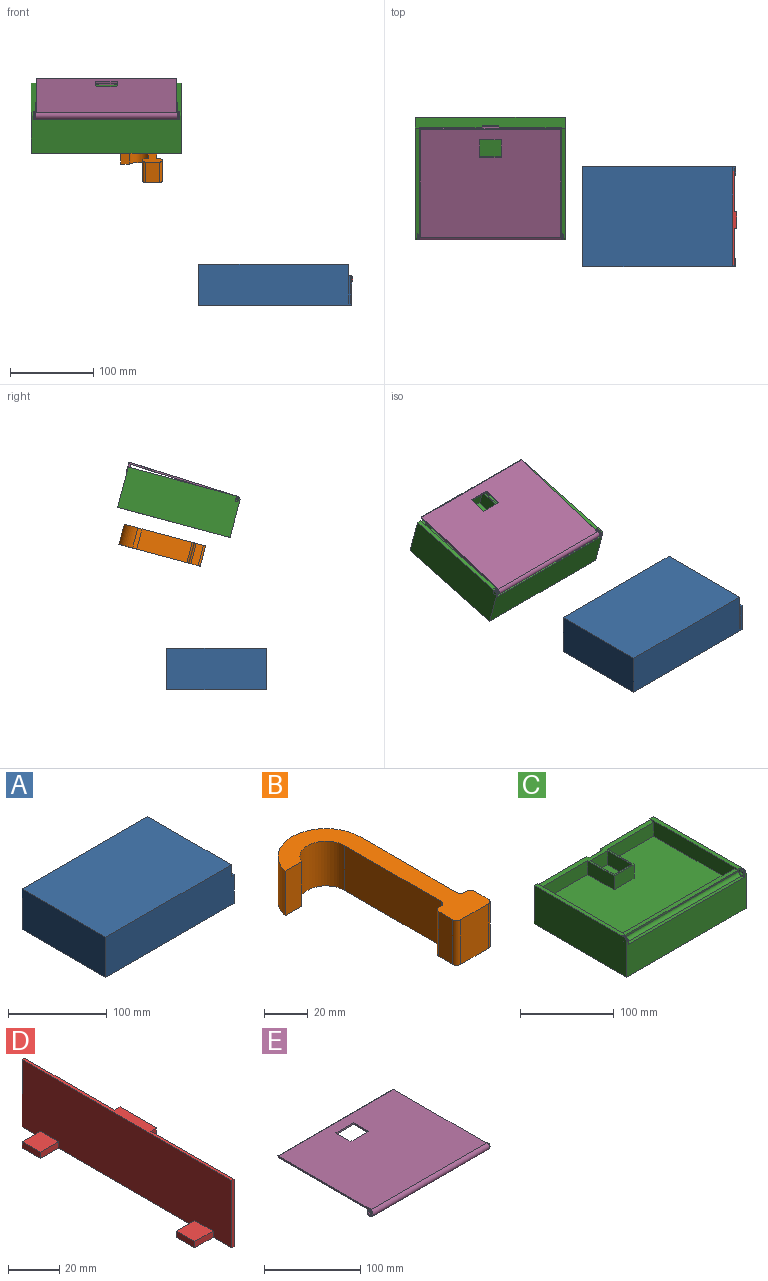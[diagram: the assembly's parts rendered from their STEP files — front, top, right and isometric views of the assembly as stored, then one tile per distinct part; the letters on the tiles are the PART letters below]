
ASSEMBLY  parts=5 mates=3
PART A: 23 faces, bbox 184x120x50 mm
  f0: plane 120x48mm, normal (1,0,0), area 2324mm2, adj f2,f5,f6,f7,f8,f9,f10,f12
  f1: plane 100x2mm, normal (1,0,0), area 200mm2, adj f4,f9,f14,f18
  f2: plane 180x120mm, normal (0,0,1), area 21600mm2, adj f0,f3,f5,f6
  f3: plane 120x50mm, normal (-1,0,0), area 6000mm2, adj f2,f4,f5,f6
  f4: plane 184x120mm, normal (0,0,-1), area 20772.1mm2, adj f1,f3,f5,f6,f14,f15,f17,f18
  f5: plane 184x50mm, normal (0,-1,0), area 9144mm2, adj f0,f2,f3,f4,f15,f16
  f6: plane 184x50mm, normal (0,1,0), area 9144mm2, adj f0,f2,f3,f4,f17,f21
  f7: plane 175x110mm, normal (0,0,-1), area 19250mm2, adj f0,f8,f10,f11
  f8: plane 175x30mm, normal (0,1,0), area 5250mm2, adj f0,f7,f9,f11
  f9: plane 177x116mm, normal (0,0,1), area 18374.1mm2, adj f0,f1,f8,f10,f11,f12,f13,f14
  f10: plane 175x30mm, normal (0,-1,0), area 5250mm2, adj f0,f7,f9,f11
  f11: plane 110x30mm, normal (1,0,0), area 3300mm2, adj f7,f8,f9,f10
  f12: plane 34x2mm, normal (0,1,0), area 68mm2, adj f0,f9,f13,f16
  f13: plane 34x8mm, normal (-1,0,0), area 272mm2, adj f9,f12,f14,f16
  f14: plane 36x4mm, normal (0,1,0), area 76mm2, adj f1,f4,f9,f13,f15,f16
  f15: plane 36x10mm, normal (1,0,0), area 360mm2, adj f4,f5,f14,f16
  f16: plane 10x4mm, normal (0,0,1), area 24mm2, adj f0,f5,f12,f13,f14,f15
  f17: plane 36x10mm, normal (1,0,0), area 360mm2, adj f4,f6,f18,f21
  f18: plane 36x4mm, normal (0,-1,0), area 76mm2, adj f1,f4,f9,f17,f19,f21
  f19: plane 34x8mm, normal (-1,0,0), area 272mm2, adj f9,f18,f20,f21
  f20: plane 34x2mm, normal (0,-1,0), area 68mm2, adj f0,f9,f19,f21
  f21: plane 10x4mm, normal (0,0,1), area 24mm2, adj f0,f6,f17,f18,f19,f20
  f22: cylinder r=17mm len=34mm, axis (0,0,-1), area 213.6mm2, adj f4,f9
PART B: 18 faces, bbox 49.9x101x25 mm
  f0: plane 25x17.98mm, normal (0,-1,0), area 449.5mm2, adj f1,f15,f16,f17
  f1: cylinder r=2.5mm len=25mm, axis (0,0,1), area 98.2mm2, adj f0,f2,f16,f17
  f2: plane 25x9mm, normal (-1,0,0), area 225mm2, adj f1,f3,f16,f17
  f3: cylinder r=2.5mm len=25mm, axis (0,0,1), area 98.2mm2, adj f2,f4,f16,f17
  f4: plane 25x1.5mm, normal (0,1,0), area 37.5mm2, adj f3,f5,f16,f17
  f5: cylinder r=2.5mm len=25mm, axis (0,0,1), area 98.2mm2, adj f4,f6,f16,f17
  f6: plane 62.5x25mm, normal (-1,0,0), area 1562.5mm2, adj f5,f7,f16,f17
  f7: cylinder r=12mm len=25mm, axis (0,0,1), area 813.9mm2, adj f6,f8,f16,f17
  f8: plane 25x10.49mm, normal (0,-1,0), area 262.3mm2, adj f7,f9,f16,f17
  f9: cylinder r=21.98mm len=43.39mm, axis (0,0,1), area 1600.5mm2, adj f8,f10,f16,f17
  f10: plane 62.5x25mm, normal (1,0,0), area 1562.5mm2, adj f9,f11,f16,f17
  f11: cylinder r=2.5mm len=25mm, axis (0,0,1), area 98.2mm2, adj f10,f12,f16,f17
  f12: plane 25x1.5mm, normal (0,1,0), area 37.5mm2, adj f11,f13,f16,f17
  f13: cylinder r=2.5mm len=25mm, axis (0,0,1), area 98.2mm2, adj f12,f14,f16,f17
  f14: plane 25x9mm, normal (1,0,0), area 225mm2, adj f13,f15,f16,f17
  f15: cylinder r=2.5mm len=25mm, axis (0,0,1), area 98.2mm2, adj f0,f14,f16,f17
  f16: plane 100.98x49.89mm, normal (0,0,-1), area 1449.7mm2, adj f0,f1,f2,f3,f4,f5,f6,f7
  f17: plane 100.98x49.89mm, normal (0,0,1), area 1449.7mm2, adj f0,f1,f2,f3,f4,f5,f6,f7
PART C: 107 faces, bbox 180.4x141.9x51.9 mm
  f0: plane 170x46mm, normal (0,0,1), area 1224mm2, adj f1,f3,f10,f11,f12,f13,f29,f31
  f1: plane 70x18mm, normal (0,-1,0), area 1260mm2, adj f0,f2,f31,f83
  f2: plane 170x121mm, normal (0,0,1), area 19370mm2, adj f1,f3,f29,f30,f31,f83,f84,f85
  f3: plane 70x18mm, normal (0,-1,0), area 1260mm2, adj f0,f2,f29,f84
  f4: plane 25x1.5mm, normal (0,1,0), area 37.5mm2, adj f6,f39,f52,f79
  f5: plane 25x13mm, normal (1,0,0), area 325mm2, adj f6,f62,f77,f78
  f6: plane 180x140mm, normal (0,0,-1), area 19797.4mm2, adj f4,f5,f10,f17,f18,f19,f34,f35
  f7: plane 136.01x5mm, normal (0,0,1), area 668.4mm2, adj f8,f10,f16,f19,f31,f94,f95
  f8: plane 175.6x4mm, normal (0,-1,0), area 356.3mm2, adj f7,f9,f15,f22,f24,f29,f31,f33
  f9: plane 136x5mm, normal (0,0,1), area 668.4mm2, adj f8,f10,f17,f20,f29,f99,f100
  f10: plane 180x50mm, normal (0,1,0), area 8500mm2, adj f0,f6,f7,f9,f12,f13,f17,f19
  f11: plane 20x8mm, normal (0,1,0), area 136mm2, adj f0,f12,f13,f32,f104,f105,f106
  f12: plane 8x3mm, normal (1,0,0), area 24mm2, adj f0,f10,f11,f32
  f13: plane 8x3mm, normal (-1,0,0), area 24mm2, adj f0,f10,f11,f32
  f14: plane 3.2x1.6mm, normal (1,0,0), area 1.5mm2, adj f21,f28,f96
  f15: plane 3.2x1.6mm, normal (-1,0,0), area 1.5mm2, adj f8,f27,f95
  f16: cylinder r=4mm len=4mm, axis (-1,0,0), area 11.9mm2, adj f7,f18,f19,f93
  f17: plane 140x50mm, normal (-1,0,0), area 6996.6mm2, adj f6,f9,f10,f18,f20
  f18: plane 180x46.01mm, normal (0,-1,0), area 7576.9mm2, adj f6,f16,f17,f19,f20,f21,f91,f92
  f19: plane 140x50mm, normal (1,0,0), area 6996.6mm2, adj f6,f7,f10,f16,f18
  f20: cylinder r=4mm len=4mm, axis (-1,0,0), area 11.9mm2, adj f9,f17,f18,f98
  f21: plane 175.6x4mm, normal (0,0,1), area 696.3mm2, adj f14,f18,f23,f24,f91,f96
  f22: plane 3.2x1.6mm, normal (1,0,0), area 1.5mm2, adj f8,f28,f100
  f23: plane 3.2x1.6mm, normal (-1,0,0), area 1.5mm2, adj f21,f27,f91
  f24: cylinder r=4mm len=174mm, axis (1,0,0), area 1093.3mm2, adj f8,f21,f27,f28
  f25: plane 4x4mm, normal (1,0,0), area 12.6mm2, adj f28
  f26: plane 4x4mm, normal (-1,0,0), area 12.6mm2, adj f27
  f27: torus R=4mm, axis (1,0,0), area 42.9mm2, adj f15,f23,f24,f26,f92,f93,f94
  f28: torus R=4mm, axis (1,0,0), area 42.9mm2, adj f14,f22,f24,f25,f97,f98,f99
  f29: plane 132x20mm, normal (1,0,0), area 2442mm2, adj f0,f2,f3,f8,f9,f10,f30,f33
  f30: plane 170x18mm, normal (0,1,0), area 3060mm2, adj f2,f29,f31,f33
  f31: plane 132x20mm, normal (-1,0,0), area 2442mm2, adj f0,f1,f2,f7,f8,f10,f30,f33
  f32: plane 20x5mm, normal (0,0,1), area 72.4mm2, adj f10,f11,f12,f13,f80,f81,f102,f105
  f33: plane 170x5mm, normal (0,0,1), area 850mm2, adj f8,f29,f30,f31
  f34: plane 63x25mm, normal (-1,0,0), area 1575mm2, adj f6,f35,f51,f52
  f35: cylinder r=2mm len=25mm, axis (0,0,-1), area 78.5mm2, adj f6,f34,f36,f52
  f36: plane 25x3mm, normal (0,-1,0), area 75mm2, adj f6,f35,f37,f52
  f37: cylinder r=2mm len=25mm, axis (0,0,-1), area 78.5mm2, adj f6,f36,f38,f52
  f38: plane 25x11mm, normal (-1,0,0), area 275mm2, adj f6,f37,f39,f52
  f39: cylinder r=2mm len=25mm, axis (0,0,-1), area 78.5mm2, adj f4,f6,f38,f52
  f40: plane 25x1.5mm, normal (0,1,0), area 37.5mm2, adj f6,f41,f52,f79
  f41: cylinder r=2mm len=25mm, axis (0,0,-1), area 78.5mm2, adj f6,f40,f42,f52
  f42: plane 25x11mm, normal (1,0,0), area 275mm2, adj f6,f41,f43,f52
  f43: cylinder r=2mm len=25mm, axis (0,0,-1), area 78.5mm2, adj f6,f42,f44,f52
  f44: plane 25x3mm, normal (0,-1,0), area 75mm2, adj f6,f43,f45,f52
  f45: cylinder r=2mm len=25mm, axis (0,0,-1), area 78.5mm2, adj f6,f44,f46,f52
  f46: plane 63x25mm, normal (1,0,0), area 1575mm2, adj f6,f45,f47,f52
  f47: cylinder r=11mm len=25mm, axis (0,0,-1), area 821.5mm2, adj f6,f46,f48,f52
  f48: cylinder r=2mm len=25mm, axis (0,0,-1), area 70.8mm2, adj f6,f47,f49,f52
  f49: plane 25x7.05mm, normal (0,1,0), area 176.4mm2, adj f6,f48,f50,f52
  f50: cylinder r=2mm len=25mm, axis (0,0,-1), area 83.5mm2, adj f6,f49,f51,f52
  f51: cylinder r=22mm len=43.89mm, axis (0,0,-1), area 1672.8mm2, adj f6,f34,f50,f52
  f52: plane 107x50.9mm, normal (0,0,-1), area 1727.5mm2, adj f4,f34,f35,f36,f37,f38,f39,f40
  f53: plane 25x21mm, normal (0,-1,0), area 525mm2, adj f6,f54,f76,f77
  f54: cylinder r=2mm len=25mm, axis (0,0,-1), area 78.5mm2, adj f6,f53,f55,f77
  f55: plane 25x3mm, normal (-1,0,0), area 75mm2, adj f6,f54,f56,f77
  f56: cylinder r=2mm len=25mm, axis (0,0,-1), area 78.5mm2, adj f6,f55,f57,f77
  f57: plane 25x21mm, normal (0,1,0), area 525mm2, adj f6,f56,f58,f77
  f58: cylinder r=2mm len=25mm, axis (0,0,-1), area 78.5mm2, adj f6,f57,f59,f77
  f59: plane 25x6mm, normal (-1,0,0), area 150mm2, adj f6,f58,f60,f77
  f60: cylinder r=2mm len=25mm, axis (0,0,-1), area 78.5mm2, adj f6,f59,f61,f77
  f61: plane 61x25mm, normal (0,1,0), area 1525mm2, adj f6,f60,f62,f77
  f62: cylinder r=2mm len=25mm, axis (0,0,-1), area 78.5mm2, adj f5,f6,f61,f77
  f63: plane 25x13mm, normal (1,0,0), area 325mm2, adj f6,f64,f77,f78
  f64: cylinder r=2mm len=25mm, axis (0,0,-1), area 78.5mm2, adj f6,f63,f65,f77
  f65: plane 61x25mm, normal (0,-1,0), area 1525mm2, adj f6,f64,f66,f77
  f66: cylinder r=2mm len=25mm, axis (0,0,-1), area 78.5mm2, adj f6,f65,f67,f77
  f67: plane 25x6mm, normal (-1,0,0), area 150mm2, adj f6,f66,f68,f77
  f68: cylinder r=2mm len=25mm, axis (0,0,-1), area 78.5mm2, adj f6,f67,f69,f77
  f69: plane 25x21mm, normal (0,-1,0), area 525mm2, adj f6,f68,f70,f77
  f70: cylinder r=2mm len=25mm, axis (0,0,-1), area 78.5mm2, adj f6,f69,f71,f77
  f71: plane 25x3mm, normal (-1,0,0), area 75mm2, adj f6,f70,f72,f77
  f72: cylinder r=2mm len=25mm, axis (0,0,-1), area 78.5mm2, adj f6,f71,f73,f77
  f73: plane 25x21mm, normal (0,1,0), area 525mm2, adj f6,f72,f74,f77
  f74: cylinder r=2mm len=25mm, axis (0,0,-1), area 78.5mm2, adj f6,f73,f75,f77
  f75: plane 25x12mm, normal (-1,0,0), area 300mm2, adj f6,f74,f76,f77
  f76: cylinder r=2mm len=25mm, axis (0,0,-1), area 78.5mm2, adj f6,f53,f75,f77
  f77: plane 95x50mm, normal (0,0,-1), area 3675.1mm2, adj f5,f53,f54,f55,f56,f57,f58,f59
  f78: extruded ~25x20mm, area 605.5mm2, adj f5,f6,f63,f77
  f79: extruded ~25x18mm, area 561.1mm2, adj f4,f6,f40,f52
  f80: plane 2x1mm, normal (-1,0,0), area 2mm2, adj f32,f82,f103,f106
  f81: plane 2x1mm, normal (1,0,0), area 2mm2, adj f32,f82,f101,f105
  f82: plane 6x1mm, normal (0,0,-1), area 6mm2, adj f80,f81,f102,f104
  f83: plane 40x18mm, normal (1,0,0), area 720mm2, adj f0,f1,f2,f85
  f84: plane 40x18mm, normal (-1,0,0), area 720mm2, adj f0,f2,f3,f85
  f85: plane 30x18mm, normal (0,-1,0), area 540mm2, adj f0,f2,f83,f84
  f86: plane 26x18mm, normal (0,1,0), area 468mm2, adj f0,f87,f89,f90
  f87: plane 36x18mm, normal (-1,0,0), area 648mm2, adj f0,f86,f88,f90
  f88: plane 26x18mm, normal (0,-1,0), area 468mm2, adj f0,f87,f89,f90
  f89: plane 36x18mm, normal (1,0,0), area 648mm2, adj f0,f86,f88,f90
  f90: plane 36x26mm, normal (0,0,1), area 936mm2, adj f86,f87,f88,f89
  f91: cylinder r=0.8mm len=1.6mm, axis (0,0,-1), area 2mm2, adj f18,f21,f23,f92
  f92: bspline ~3.43x1.79mm, area 3.8mm2, adj f18,f27,f91,f93
  f93: torus R=3.2mm, axis (-1,0,0), area 10mm2, adj f16,f27,f92,f94
  f94: bspline ~3.43x1.79mm, area 3.8mm2, adj f7,f27,f93,f95
  f95: cylinder r=0.8mm len=1.6mm, axis (0,-1,0), area 2mm2, adj f7,f8,f15,f94
  f96: cylinder r=0.8mm len=1.6mm, axis (0,0,1), area 2mm2, adj f14,f18,f21,f97
  f97: bspline ~3.32x1.79mm, area 3.8mm2, adj f18,f28,f96,f98
  f98: torus R=3.2mm, axis (-1,0,0), area 10mm2, adj f20,f28,f97,f99
  f99: bspline ~3.32x1.79mm, area 3.8mm2, adj f9,f28,f98,f100
  f100: cylinder r=0.8mm len=1.6mm, axis (0,1,0), area 2mm2, adj f8,f9,f22,f99
  f101: cylinder r=1mm len=2mm, axis (0,0,-1), area 1.6mm2, adj f81,f102
  f102: cylinder r=1mm len=6mm, axis (-1,0,0), area 15.7mm2, adj f32,f82,f101,f103
  f103: cylinder r=1mm len=2mm, axis (0,0,1), area 1.6mm2, adj f80,f102
  f104: cylinder r=1mm len=8mm, axis (1,0,0), area 11mm2, adj f11,f82,f105,f106
  f105: cylinder r=1mm len=3mm, axis (0,0,1), area 3.9mm2, adj f11,f32,f81,f104
  f106: cylinder r=1mm len=3mm, axis (0,0,-1), area 3.9mm2, adj f11,f32,f80,f104
PART D: 18 faces, bbox 14.5x115x32 mm
  f0: plane 115x32mm, normal (-1,0,0), area 3620mm2, adj f1,f2,f4,f5,f10,f11,f12,f14
  f1: plane 32x1.5mm, normal (0,-1,0), area 48mm2, adj f0,f3,f4,f5
  f2: plane 32x1.5mm, normal (0,1,0), area 48mm2, adj f0,f3,f4,f5
  f3: plane 115x32mm, normal (1,0,0), area 3567.5mm2, adj f1,f2,f4,f5,f6,f7,f8
  f4: plane 115x4.5mm, normal (0,0,1), area 232.5mm2, adj f0,f1,f2,f3,f6,f8,f9
  f5: plane 115x11.5mm, normal (0,0,-1), area 372.5mm2, adj f0,f1,f2,f3,f10,f12,f13,f14
  f6: plane 5.62x3mm, normal (0,-1,0), area 16.9mm2, adj f3,f4,f7,f9
  f7: plane 20x3mm, normal (0,0,-1), area 60mm2, adj f3,f6,f8,f9
  f8: plane 5.62x3mm, normal (0,1,0), area 16.9mm2, adj f3,f4,f7,f9
  f9: plane 20x5.62mm, normal (1,0,0), area 112.5mm2, adj f4,f6,f7,f8
  f10: plane 10x3mm, normal (0,-1,0), area 30mm2, adj f0,f5,f11,f13
  f11: plane 10x10mm, normal (0,0,1), area 100mm2, adj f0,f10,f12,f13
  f12: plane 10x3mm, normal (0,1,0), area 30mm2, adj f0,f5,f11,f13
  f13: plane 10x3mm, normal (-1,0,0), area 30mm2, adj f5,f10,f11,f12
  f14: plane 10x3mm, normal (0,-1,0), area 30mm2, adj f0,f5,f15,f17
  f15: plane 10x10mm, normal (0,0,1), area 100mm2, adj f0,f14,f16,f17
  f16: plane 10x3mm, normal (0,1,0), area 30mm2, adj f0,f5,f15,f17
  f17: plane 10x3mm, normal (-1,0,0), area 30mm2, adj f5,f14,f15,f16
PART E: 35 faces, bbox 177x141.3x10.3 mm
  f0: plane 169x132.54mm, normal (0,0,-1), area 21786.6mm2, adj f3,f4,f5,f7,f8,f9,f21,f22
  f1: plane 169x136mm, normal (0,0,1), area 22412mm2, adj f3,f4,f9,f21,f22,f23,f24,f31
  f2: plane 18x8mm, normal (0,1,0), area 144mm2, adj f29,f31,f32,f33
  f3: plane 136x2mm, normal (-1,0,0), area 267.1mm2, adj f0,f1,f9,f30
  f4: plane 136x2mm, normal (1,0,0), area 267.1mm2, adj f0,f1,f9,f34
  f5: plane 20x8mm, normal (0,-1,0), area 155mm2, adj f0,f6,f7,f8,f18,f19,f20
  f6: plane 20x3mm, normal (0,0,-1), area 45mm2, adj f5,f7,f8,f19,f20,f28,f32
  f7: plane 8x2mm, normal (1,0,0), area 16mm2, adj f0,f5,f6,f33
  f8: plane 8x2mm, normal (-1,0,0), area 16mm2, adj f0,f5,f6,f29
  f9: cylinder r=4mm len=171mm, axis (-1,0,0), area 3589.8mm2, adj f0,f1,f3,f4,f25,f26
  f10: plane 6x6mm, normal (1,0,0), area 15.7mm2, adj f12,f25
  f11: plane 6x6mm, normal (-1,0,0), area 15.7mm2, adj f15,f26
  f12: cylinder r=2mm len=4mm, axis (-1,0,0), area 6.3mm2, adj f10,f14
  f13: plane 1x1mm, normal (1,0,0), area 0.8mm2, adj f14
  f14: torus R=0.5mm, axis (1,0,0), area 21.5mm2, adj f12,f13
  f15: cylinder r=2mm len=4mm, axis (1,0,0), area 6.3mm2, adj f11,f17
  f16: plane 1x1mm, normal (-1,0,0), area 0.8mm2, adj f17
  f17: torus R=0.5mm, axis (-1,0,0), area 21.5mm2, adj f15,f16
  f18: plane 5x1mm, normal (0,0,1), area 5mm2, adj f5,f19,f20,f27
  f19: plane 1.87x1mm, normal (-1,0,0), area 1.6mm2, adj f5,f6,f18,f27,f28
  f20: plane 1.87x1mm, normal (1,0,0), area 1.6mm2, adj f5,f6,f18,f27,f28
  f21: plane 26x2mm, normal (0,-1,0), area 52mm2, adj f0,f1,f22,f24
  f22: plane 22x2mm, normal (1,0,0), area 44mm2, adj f0,f1,f21,f23
  f23: plane 26x2mm, normal (0,1,0), area 52mm2, adj f0,f1,f22,f24
  f24: plane 22x2mm, normal (-1,0,0), area 44mm2, adj f0,f1,f21,f23
  f25: torus R=3mm, axis (1,0,0), area 35.9mm2, adj f9,f10
  f26: torus R=3mm, axis (1,0,0), area 35.9mm2, adj f9,f11
  f27: cylinder r=1mm len=5mm, axis (1,0,0), area 5.2mm2, adj f18,f19,f20,f28
  f28: cylinder r=1mm len=5mm, axis (-1,0,0), area 5.2mm2, adj f6,f19,f20,f27
  f29: cylinder r=1mm len=9mm, axis (0,0,1), area 12.6mm2, adj f2,f8,f31,f32
  f30: cylinder r=1mm len=2mm, axis (0,0,1), area 2mm2, adj f3,f31
  f31: cylinder r=1mm len=169mm, axis (-1,0,0), area 498.4mm2, adj f0,f1,f2,f29,f30,f33,f34
  f32: cylinder r=1mm len=20mm, axis (-1,0,0), area 30.3mm2, adj f2,f6,f29,f33
  f33: cylinder r=1mm len=9mm, axis (0,0,-1), area 12.6mm2, adj f2,f7,f31,f32
  f34: cylinder r=1mm len=2mm, axis (0,0,-1), area 2mm2, adj f4,f31
PLACE A t=(109.01,-180.17,-173.79)mm
PLACE B rot(axis=(1,0,0),15deg) t=(126,-100.92,16.74)mm
PLACE C rot(axis=(1,0,0),15deg) t=(-98.64,-128.65,27.54)mm
PLACE D t=(53.07,-184.27,-170.79)mm
PLACE E rot(axis=(1,0,0),17.5deg) t=(-98.64,-110.75,2.62)mm
MATE slider A.f20 <-> D.f2  axis (0,-1,0) through (193.41,-122.17,-154.59)mm
MATE slider C.f52 <-> B.f17  axis (0,0.26,-0.97) through (-48.2,-131.74,52.59)mm
MATE revolute E.f9 <-> C.f16  axis (-1,0,0) through (-185.64,-204.31,54.89)mm
